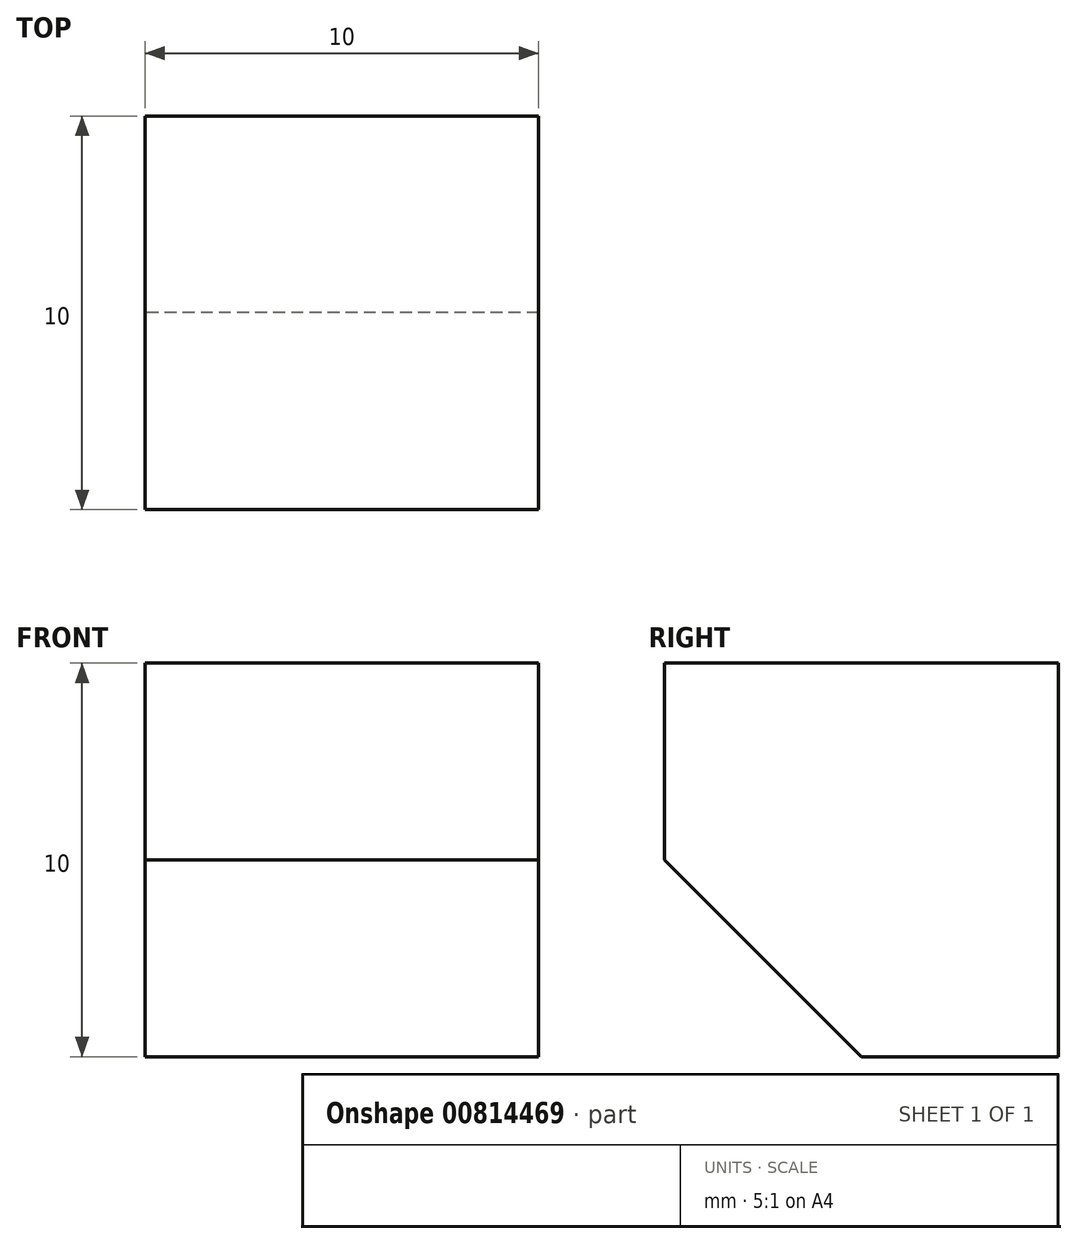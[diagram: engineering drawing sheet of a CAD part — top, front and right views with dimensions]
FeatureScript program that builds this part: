
annotation { "Feature Type Name" : "Feature", "Feature Type Description" : "" }
export const myFeature = defineFeature(function(context is Context, id is Id, definition is map)
    precondition{}
    {
        {
            var Q0;
            Q0=qCreatedBy(makeId("Right.planeOp"),FACE);
            var sketch = newSketch(context, id + "F0", { "sketchPlane" : qUnion([Q0])});
            skLineSegment(sketch, "E0.bottom", {"start": v(0, 0) * mm, "end": v(10, 0) * mm});
            skLineSegment(sketch, "E0.top", {"start": v(0, 5) * mm, "end": v(10, 5) * mm});
            skLineSegment(sketch, "E0.left", {"start": v(0, 0) * mm, "end": v(0, 5) * mm});
            skLineSegment(sketch, "E0.right", {"start": v(10, 0) * mm, "end": v(10, 5) * mm});
            skLineSegment(sketch, "E1", {"start": v(10, 0) * mm, "end": v(10, -5) * mm});
            skLineSegment(sketch, "E2", {"start": v(10, -5) * mm, "end": v(5, -5) * mm});
            skPoint(sketch, "E2.endSnap0", {"position": v(5, 0) * mm});
            skLineSegment(sketch, "E3", {"start": v(5, -5) * mm, "end": v(0, 0) * mm});
            skSolve(sketch);
        }
        {
            var Q0;
            Q0 = qSketchRegion(id + "F0", true);
            extrude(context, id + "F1", {"entities" : qUnion([Q0]), "depth" : 10 * mm, "offsetDistance" : 25 * mm, "symmetric" : true});
        }
        {
            var Q0;
            Q0=makeQuery(id+"F1.opExtrude","CAP_EDGE",EDGE,{"disambiguationData":[OSD([sQuery(id+"F0.wireOp",EDGE,"E0.top")])],"isStart":false});
            cPoint(context, id + "F2", {"entities" : qUnion([Q0]), "parameter" : 0.5});
        }
        {
            var Q0;
            Q0=makeQuery(id+"F1.opExtrude","SWEPT_EDGE",EDGE,{"disambiguationData":[OSD([sQuery(id+"F0.wireOp",EDGE,"E0.top"),sQuery(id+"F0.wireOp",EDGE,"E0.left")])]});
            cPoint(context, id + "F3", {"entities" : qUnion([Q0]), "parameter" : 0.5});
        }
        {
            var Q0;
            Q0 = qCreatedBy(id + "F2" ,VERTEX);
            var Q1;
            Q1 = qCreatedBy(id + "F3" ,VERTEX);
            var Q2;
            Q2=makeQuery(id+"F1.opExtrude","CAP_VERTEX",VERTEX,{"disambiguationData":[OSD([sQuery(id+"F0.wireOp",EDGE,"E0.bottom"),sQuery(id+"F0.wireOp",EDGE,"E0.left")])],"isStart":false});
            cPlane(context, id + "F4", {"entities" : qUnion([Q0, Q1, Q2]), "cplaneType" : CPlaneType.THREE_POINT, "offset" : 25 * mm, "width" : 150 * mm, "height" : 150 * mm});
        }
        {
            var Q0;
            Q0=qCreatedBy(id+"F4.planeOp",FACE);
            var sketch = newSketch(context, id + "F5", { "sketchPlane" : qUnion([Q0])});
            skPoint(sketch, "E4.0", {"position": v(-2.04, -3.54) * mm});
            skPoint(sketch, "E5.0", {"position": v(4.08, -7.07) * mm});
            skPoint(sketch, "E6.0", {"position": v(4.08, 0) * mm});
            skLineSegment(sketch, "E7", {"start": v(-2.04, -3.54) * mm, "end": v(4.08, -7.07) * mm});
            skLineSegment(sketch, "E8", {"start": v(4.08, -7.07) * mm, "end": v(4.08, 0) * mm});
            skLineSegment(sketch, "E9", {"start": v(4.08, 0) * mm, "end": v(-2.04, -3.54) * mm});
            skSolve(sketch);
        }
        {
            var Q0;
            Q0 = qSketchRegion(id + "F5", true);
            extrude(context, id + "F6", {"entities" : qUnion([Q0]), "operationType" : NewBodyOperationType.REMOVE, "endBound" : BoundingType.THROUGH_ALL, "oppositeDirection" : true, "depth" : 25 * mm, "offsetDistance" : 25 * mm});
        }
    });
